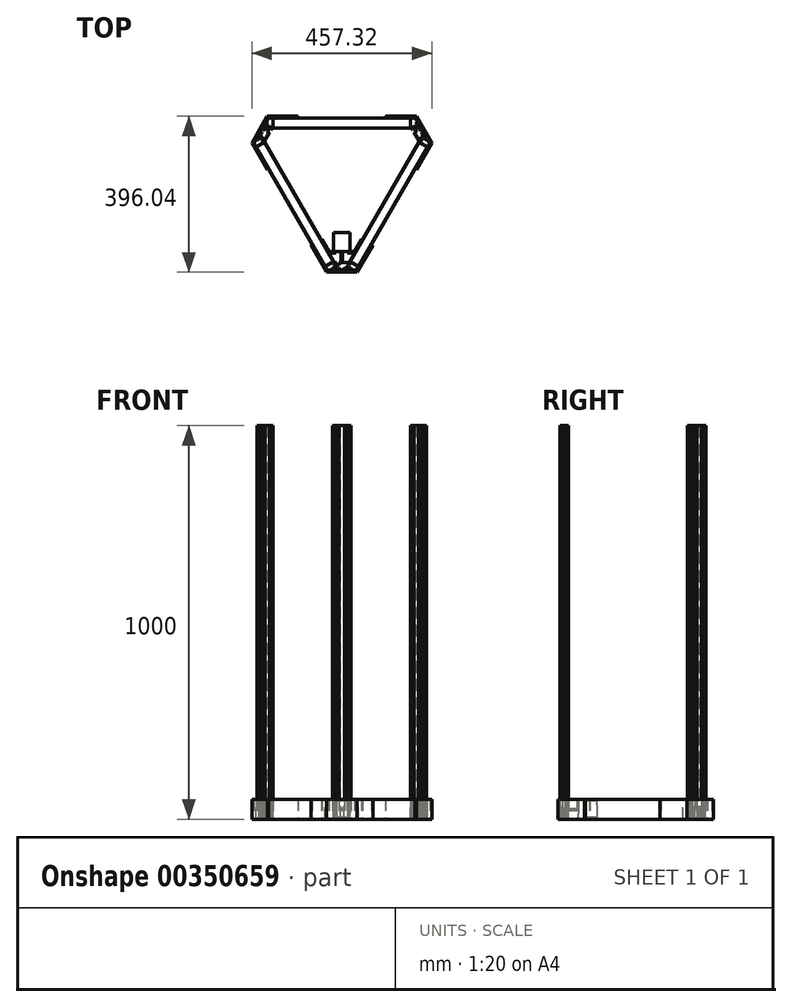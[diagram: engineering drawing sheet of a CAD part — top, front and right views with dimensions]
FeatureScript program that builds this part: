
annotation { "Feature Type Name" : "Feature", "Feature Type Description" : "" }
export const myFeature = defineFeature(function(context is Context, id is Id, definition is map)
    precondition{}
    {
        {
            var Q0;
            Q0=qCreatedBy(makeId("Top.planeOp"),FACE);
            var sketch = newSketch(context, id + "F0", { "sketchPlane" : qUnion([Q0])});
            skLineSegment(sketch, "E0", {"start": v(-75.18, 65.27) * mm, "end": v(-37.5, 0) * mm});
            skLineSegment(sketch, "E1", {"start": v(37.5, 0) * mm, "end": v(75.18, 65.27) * mm});
            skLineSegment(sketch, "E2.0", {"start": v(39.23, -5) * mm, "end": v(78.65, 63.27) * mm});
            skLineSegment(sketch, "E2.2", {"start": v(-78.65, 63.27) * mm, "end": v(-39.23, -5) * mm});
            skLineSegment(sketch, "E3", {"start": v(-78.65, 63.27) * mm, "end": v(-75.18, 65.27) * mm});
            skLineSegment(sketch, "E4", {"start": v(75.18, 65.27) * mm, "end": v(78.65, 63.27) * mm});
            skLineSegment(sketch, "E5", {"start": v(-39.23, -5) * mm, "end": v(39.23, -5) * mm});
            skLineSegment(sketch, "E6", {"start": v(-23.5, 0) * mm, "end": v(-23.5, 7) * mm});
            skLineSegment(sketch, "E7", {"start": v(-23.5, 7) * mm, "end": v(-20, 7) * mm});
            skLineSegment(sketch, "E8", {"start": v(-20, 7) * mm, "end": v(-20, 0) * mm});
            skLineSegment(sketch, "E9", {"start": v(-20, 0) * mm, "end": v(20, 0) * mm});
            skLineSegment(sketch, "E10", {"start": v(20, 0) * mm, "end": v(20, 7) * mm});
            skLineSegment(sketch, "E11", {"start": v(20, 7) * mm, "end": v(23.5, 7) * mm});
            skLineSegment(sketch, "E12", {"start": v(23.5, 7) * mm, "end": v(23.5, 0) * mm});
            skLineSegment(sketch, "E13", {"start": v(-37.5, 0) * mm, "end": v(-23.5, 0) * mm});
            skLineSegment(sketch, "E14", {"start": v(23.5, 0) * mm, "end": v(37.5, 0) * mm});
            skSolve(sketch);
        }
        {
            var Q0;
            Q0 = qSketchRegion(id + "F0", true);
            extrude(context, id + "F1", {"entities" : qUnion([Q0]), "depth" : 50.8 * mm});
        }
        {
            var Q0;
            Q0=qCreatedBy(makeId("Top.planeOp"),FACE);
            var sketch = newSketch(context, id + "F2", { "sketchPlane" : qUnion([Q0])});
            skLineSegment(sketch, "E15", {"start": v(-20, 22.38) * mm, "end": v(-20.8, 22.38) * mm});
            skLineSegment(sketch, "E16", {"start": v(-20.8, 22.38) * mm, "end": v(-23.17, 20) * mm});
            skLineSegment(sketch, "E17", {"start": v(-23.17, 20) * mm, "end": v(-20.8, 17.63) * mm});
            skLineSegment(sketch, "E18", {"start": v(-20.8, 17.63) * mm, "end": v(-20, 17.63) * mm});
            skLineSegment(sketch, "E19", {"start": v(-20, 17.63) * mm, "end": v(-20, 13) * mm});
            skLineSegment(sketch, "E20", {"start": v(-20, 13) * mm, "end": v(-18, 13) * mm});
            skLineSegment(sketch, "E21", {"start": v(-18, 13) * mm, "end": v(-18, 16) * mm});
            skLineSegment(sketch, "E22", {"start": v(-18, 16) * mm, "end": v(-17.06, 16) * mm});
            skLineSegment(sketch, "E23", {"start": v(-17.06, 16) * mm, "end": v(-14, 12.94) * mm});
            skLineSegment(sketch, "E24", {"start": v(-14, 12.94) * mm, "end": v(-14, 7.06) * mm});
            skLineSegment(sketch, "E25", {"start": v(-14, 7.06) * mm, "end": v(-17.06, 4) * mm});
            skLineSegment(sketch, "E26", {"start": v(-17.06, 4) * mm, "end": v(-18, 4) * mm});
            skLineSegment(sketch, "E27", {"start": v(-18, 4) * mm, "end": v(-18, 7) * mm});
            skLineSegment(sketch, "E28", {"start": v(-18, 7) * mm, "end": v(-20, 7) * mm});
            skLineSegment(sketch, "E29", {"start": v(-20, 7) * mm, "end": v(-20, 0) * mm});
            skLineSegment(sketch, "E30", {"start": v(-20, 0) * mm, "end": v(-13, 0) * mm});
            skLineSegment(sketch, "E31", {"start": v(-13, 0) * mm, "end": v(-13, 2) * mm});
            skLineSegment(sketch, "E32", {"start": v(-13, 2) * mm, "end": v(-16, 2) * mm});
            skLineSegment(sketch, "E33", {"start": v(-16, 2) * mm, "end": v(-16, 2.94) * mm});
            skLineSegment(sketch, "E34", {"start": v(-16, 2.94) * mm, "end": v(-12.94, 6) * mm});
            skLineSegment(sketch, "E35", {"start": v(-12.94, 6) * mm, "end": v(-7.06, 6) * mm});
            skLineSegment(sketch, "E36", {"start": v(-7.06, 6) * mm, "end": v(-4, 2.94) * mm});
            skLineSegment(sketch, "E37", {"start": v(-4, 2.94) * mm, "end": v(-4, 2) * mm});
            skLineSegment(sketch, "E38", {"start": v(-4, 2) * mm, "end": v(-7, 2) * mm});
            skLineSegment(sketch, "E39", {"start": v(-7, 2) * mm, "end": v(-7, 0) * mm});
            skLineSegment(sketch, "E40", {"start": v(-7, 0) * mm, "end": v(7, 0) * mm});
            skLineSegment(sketch, "E41", {"start": v(7, 0) * mm, "end": v(7, 2) * mm});
            skLineSegment(sketch, "E42", {"start": v(7, 2) * mm, "end": v(4, 2) * mm});
            skLineSegment(sketch, "E43", {"start": v(4, 2) * mm, "end": v(4, 2.94) * mm});
            skLineSegment(sketch, "E44", {"start": v(4, 2.94) * mm, "end": v(7.06, 6) * mm});
            skLineSegment(sketch, "E45", {"start": v(7.06, 6) * mm, "end": v(12.94, 6) * mm});
            skLineSegment(sketch, "E46", {"start": v(12.94, 6) * mm, "end": v(16, 2.94) * mm});
            skLineSegment(sketch, "E47", {"start": v(16, 2) * mm, "end": v(13, 2) * mm});
            skLineSegment(sketch, "E48", {"start": v(13, 2) * mm, "end": v(13, 0) * mm});
            skLineSegment(sketch, "E49", {"start": v(13, 0) * mm, "end": v(20, 0) * mm});
            skLineSegment(sketch, "E50", {"start": v(20, 0) * mm, "end": v(20, 7) * mm});
            skLineSegment(sketch, "E51", {"start": v(20, 7) * mm, "end": v(18, 7) * mm});
            skLineSegment(sketch, "E52", {"start": v(18, 7) * mm, "end": v(18, 4) * mm});
            skLineSegment(sketch, "E53", {"start": v(18, 4) * mm, "end": v(17.06, 4) * mm});
            skLineSegment(sketch, "E54", {"start": v(17.06, 4) * mm, "end": v(14, 7.06) * mm});
            skLineSegment(sketch, "E55", {"start": v(14, 7.06) * mm, "end": v(14, 12.94) * mm});
            skLineSegment(sketch, "E56", {"start": v(14, 12.94) * mm, "end": v(17.06, 16) * mm});
            skLineSegment(sketch, "E57", {"start": v(17.06, 16) * mm, "end": v(18, 16) * mm});
            skLineSegment(sketch, "E58", {"start": v(18, 16) * mm, "end": v(18, 13) * mm});
            skLineSegment(sketch, "E59", {"start": v(18, 13) * mm, "end": v(20, 13) * mm});
            skLineSegment(sketch, "E60", {"start": v(20, 13) * mm, "end": v(20, 17.63) * mm});
            skLineSegment(sketch, "E61", {"start": v(23.18, 20) * mm, "end": v(20.8, 22.38) * mm});
            skLineSegment(sketch, "E62", {"start": v(20.8, 22.38) * mm, "end": v(20, 22.38) * mm});
            skLineSegment(sketch, "E63", {"start": v(20, 22.38) * mm, "end": v(20, 20) * mm});
            skLineSegment(sketch, "E64", {"start": v(20, 20) * mm, "end": v(-7, 20) * mm});
            skLineSegment(sketch, "E65", {"start": v(-7, 20) * mm, "end": v(-7, 18) * mm});
            skLineSegment(sketch, "E66", {"start": v(-7, 18) * mm, "end": v(-4, 18) * mm});
            skLineSegment(sketch, "E67", {"start": v(-4, 18) * mm, "end": v(-4, 17.06) * mm});
            skLineSegment(sketch, "E68", {"start": v(-4, 17.06) * mm, "end": v(-7.06, 14) * mm});
            skLineSegment(sketch, "E69", {"start": v(-7.06, 14) * mm, "end": v(-12.94, 14) * mm});
            skLineSegment(sketch, "E70", {"start": v(-12.94, 14) * mm, "end": v(-16, 17.06) * mm});
            skLineSegment(sketch, "E71", {"start": v(-16, 17.06) * mm, "end": v(-16, 18) * mm});
            skLineSegment(sketch, "E72", {"start": v(-16, 18) * mm, "end": v(-13, 18) * mm});
            skLineSegment(sketch, "E73", {"start": v(-13, 18) * mm, "end": v(-13, 20) * mm});
            skLineSegment(sketch, "E74", {"start": v(-13, 20) * mm, "end": v(-20, 20) * mm});
            skLineSegment(sketch, "E75", {"start": v(-20, 20) * mm, "end": v(-20, 22.38) * mm});
            skLineSegment(sketch, "E76", {"start": v(23.18, 20) * mm, "end": v(20.8, 17.63) * mm});
            skLineSegment(sketch, "E77", {"start": v(20.8, 17.63) * mm, "end": v(20, 17.63) * mm});
            skLineSegment(sketch, "E78", {"start": v(16, 2.94) * mm, "end": v(16, 2) * mm});
            skSolve(sketch);
        }
        {
            var Q0;
            Q0 = qSketchRegion(id + "F2", true);
            extrude(context, id + "F3", {"entities" : qUnion([Q0]), "depth" : 1000 * mm});
        }
        {
            var Q0;
            Q0=makeQuery(id+"F1.opExtrude","CAP_FACE",FACE,{"disambiguationData":[OSD([sQuery(id+"F0.wireOp",EDGE,"E0"),sQuery(id+"F0.wireOp",EDGE,"E1"),sQuery(id+"F0.wireOp",EDGE,"E2.0"),sQuery(id+"F0.wireOp",EDGE,"E2.2"),sQuery(id+"F0.wireOp",EDGE,"E3"),sQuery(id+"F0.wireOp",EDGE,"E4"),sQuery(id+"F0.wireOp",EDGE,"E5"),sQuery(id+"F0.wireOp",EDGE,"E6"),sQuery(id+"F0.wireOp",EDGE,"E7"),sQuery(id+"F0.wireOp",EDGE,"E8"),sQuery(id+"F0.wireOp",EDGE,"E9"),sQuery(id+"F0.wireOp",EDGE,"E10"),sQuery(id+"F0.wireOp",EDGE,"E11"),sQuery(id+"F0.wireOp",EDGE,"E12")])],"isStart":false});
            var sketch = newSketch(context, id + "F4", { "sketchPlane" : qUnion([Q0])});
            skLineSegment(sketch, "E79", {"start": v(195.98, 325.3) * mm, "end": v(217.98, 312.6) * mm});
            skLineSegment(sketch, "E80", {"start": v(217.98, 312.6) * mm, "end": v(42.98, 9.5) * mm});
            skLineSegment(sketch, "E81", {"start": v(42.98, 9.5) * mm, "end": v(20.98, 22.2) * mm});
            skLineSegment(sketch, "E82", {"start": v(20.98, 22.2) * mm, "end": v(195.98, 325.3) * mm});
            skSolve(sketch);
        }
        {
            var Q0;
            Q0 = qSketchRegion(id + "F4", true);
            var Q1;
            Q1=sQuery(id+"F0.wireOp",VERTEX,"E4.start");
            extrude(context, id + "F5", {"entities" : qUnion([Q0]), "endBound" : BoundingType.UP_TO_VERTEX, "oppositeDirection" : true, "endBoundEntityVertex" : qUnion([Q1]), "depth" : 42.8 * mm});
        }
        {
            var Q0;
            Q0=makeQuery(id+"F5.opExtrude","SWEPT_BODY",BODY,{"disambiguationData":[OSD([sQuery(id+"F4.wireOp",EDGE,"E79"),sQuery(id+"F4.wireOp",EDGE,"E80"),sQuery(id+"F4.wireOp",EDGE,"E81"),sQuery(id+"F4.wireOp",EDGE,"E82")])]});
            var Q1;
            Q1=qCreatedBy(makeId("Right.planeOp"),FACE);
            mirror(context, id + "F6", {"entities" : qUnion([Q0]), "mirrorPlane" : qUnion([Q1])});
        }
        {
            var Q0;
            Q0=makeQuery(id+"F5.opExtrude","SWEPT_FACE",FACE,{"disambiguationData":[OSD([sQuery(id+"F4.wireOp",EDGE,"E79")])]});
            var Q1;
            Q1=makeQuery(id+"F5.opExtrude","SWEPT_FACE",FACE,{"disambiguationData":[OSD([sQuery(id+"F4.wireOp",EDGE,"E81")])]});
            cPlane(context, id + "F7", {"entities" : qUnion([Q0, Q1]), "cplaneType" : CPlaneType.MID_PLANE, "offset" : 25 * mm, "width" : 150 * mm, "height" : 150 * mm});
        }
        {
            var Q0;
            Q0=makeQuery(id+"F6.opPattern","COPY",BODY,{"derivedFrom":makeQuery(id+"F5.opExtrude","SWEPT_BODY",BODY,{"disambiguationData":[OSD([sQuery(id+"F4.wireOp",EDGE,"E79"),sQuery(id+"F4.wireOp",EDGE,"E80"),sQuery(id+"F4.wireOp",EDGE,"E81"),sQuery(id+"F4.wireOp",EDGE,"E82")])]}),"instanceName":"1"});
            var Q1;
            Q1=qCreatedBy(id+"F7.planeOp",FACE);
            mirror(context, id + "F8", {"entities" : qUnion([Q0]), "mirrorPlane" : qUnion([Q1])});
        }
        {
            var Q0;
            Q0=qCreatedBy(makeId("Top.planeOp"),FACE);
            var sketch = newSketch(context, id + "F9", { "sketchPlane" : qUnion([Q0])});
            skLineSegment(sketch, "E83", {"start": v(52.08, 76.06) * mm, "end": v(33.57, 44) * mm});
            skLineSegment(sketch, "E84", {"start": v(-33.57, 44) * mm, "end": v(-52.08, 76.06) * mm});
            skLineSegment(sketch, "E85", {"start": v(-52.08, 76.06) * mm, "end": v(-49.92, 77.31) * mm});
            skLineSegment(sketch, "E86", {"start": v(-49.92, 77.31) * mm, "end": v(-32.42, 47) * mm});
            skLineSegment(sketch, "E87", {"start": v(32.42, 47) * mm, "end": v(49.92, 77.31) * mm});
            skLineSegment(sketch, "E88", {"start": v(49.92, 77.31) * mm, "end": v(52.08, 76.06) * mm});
            skLineSegment(sketch, "E89", {"start": v(33.57, 44) * mm, "end": v(14.42, 44) * mm});
            skLineSegment(sketch, "E90", {"start": v(32.42, 47) * mm, "end": v(14.42, 47) * mm});
            skLineSegment(sketch, "E91", {"start": v(14.42, 47) * mm, "end": v(14.42, 44) * mm});
            skLineSegment(sketch, "E92", {"start": v(-33.57, 44) * mm, "end": v(-14.42, 44) * mm});
            skLineSegment(sketch, "E93", {"start": v(-32.42, 47) * mm, "end": v(-14.42, 47) * mm});
            skLineSegment(sketch, "E94", {"start": v(-14.42, 47) * mm, "end": v(-14.42, 44) * mm});
            skLineSegment(sketch, "E95", {"start": v(-14.42, 44) * mm, "end": v(14.42, 44) * mm, "construction": true});
            skSolve(sketch);
        }
        {
            var Q0;
            Q0 = qSketchRegion(id + "F9", true);
            extrude(context, id + "F10", {"entities" : qUnion([Q0]), "depth" : 50.8 * mm});
        }
        {
            var Q0;
            Q0=makeQuery(id+"F1.opExtrude","SWEPT_BODY",BODY,{"disambiguationData":[OSD([sQuery(id+"F0.wireOp",EDGE,"E0"),sQuery(id+"F0.wireOp",EDGE,"E1"),sQuery(id+"F0.wireOp",EDGE,"E2.0"),sQuery(id+"F0.wireOp",EDGE,"E2.2"),sQuery(id+"F0.wireOp",EDGE,"E3"),sQuery(id+"F0.wireOp",EDGE,"E4"),sQuery(id+"F0.wireOp",EDGE,"E5"),sQuery(id+"F0.wireOp",EDGE,"E6"),sQuery(id+"F0.wireOp",EDGE,"E7"),sQuery(id+"F0.wireOp",EDGE,"E8"),sQuery(id+"F0.wireOp",EDGE,"E9"),sQuery(id+"F0.wireOp",EDGE,"E10"),sQuery(id+"F0.wireOp",EDGE,"E11"),sQuery(id+"F0.wireOp",EDGE,"E12")])]});
            var Q1;
            Q1=qCreatedBy(id+"F7.planeOp",FACE);
            mirror(context, id + "F11", {"entities" : qUnion([Q0]), "mirrorPlane" : qUnion([Q1])});
        }
        {
            var Q0;
            Q0=makeQuery(id+"F11.opPattern","COPY",BODY,{"derivedFrom":makeQuery(id+"F1.opExtrude","SWEPT_BODY",BODY,{"disambiguationData":[OSD([sQuery(id+"F0.wireOp",EDGE,"E0"),sQuery(id+"F0.wireOp",EDGE,"E1"),sQuery(id+"F0.wireOp",EDGE,"E2.0"),sQuery(id+"F0.wireOp",EDGE,"E2.2"),sQuery(id+"F0.wireOp",EDGE,"E3"),sQuery(id+"F0.wireOp",EDGE,"E4"),sQuery(id+"F0.wireOp",EDGE,"E5"),sQuery(id+"F0.wireOp",EDGE,"E6"),sQuery(id+"F0.wireOp",EDGE,"E7"),sQuery(id+"F0.wireOp",EDGE,"E8"),sQuery(id+"F0.wireOp",EDGE,"E9"),sQuery(id+"F0.wireOp",EDGE,"E10"),sQuery(id+"F0.wireOp",EDGE,"E11"),sQuery(id+"F0.wireOp",EDGE,"E12")])]}),"instanceName":"1"});
            var Q1;
            Q1=qCreatedBy(makeId("Right.planeOp"),FACE);
            mirror(context, id + "F12", {"entities" : qUnion([Q0]), "mirrorPlane" : qUnion([Q1])});
        }
        {
            var Q0;
            Q0=makeQuery(id+"F3.opExtrude","SWEPT_BODY",BODY,{"disambiguationData":[OSD([sQuery(id+"F2.wireOp",EDGE,"E15"),sQuery(id+"F2.wireOp",EDGE,"E16"),sQuery(id+"F2.wireOp",EDGE,"E17"),sQuery(id+"F2.wireOp",EDGE,"E18"),sQuery(id+"F2.wireOp",EDGE,"E19"),sQuery(id+"F2.wireOp",EDGE,"E20"),sQuery(id+"F2.wireOp",EDGE,"E21"),sQuery(id+"F2.wireOp",EDGE,"E22"),sQuery(id+"F2.wireOp",EDGE,"E23"),sQuery(id+"F2.wireOp",EDGE,"E24"),sQuery(id+"F2.wireOp",EDGE,"E25"),sQuery(id+"F2.wireOp",EDGE,"E26"),sQuery(id+"F2.wireOp",EDGE,"E27"),sQuery(id+"F2.wireOp",EDGE,"E28"),sQuery(id+"F2.wireOp",EDGE,"E29"),sQuery(id+"F2.wireOp",EDGE,"E30"),sQuery(id+"F2.wireOp",EDGE,"E31"),sQuery(id+"F2.wireOp",EDGE,"E32"),sQuery(id+"F2.wireOp",EDGE,"E33"),sQuery(id+"F2.wireOp",EDGE,"E34"),sQuery(id+"F2.wireOp",EDGE,"E35"),sQuery(id+"F2.wireOp",EDGE,"E36"),sQuery(id+"F2.wireOp",EDGE,"E37"),sQuery(id+"F2.wireOp",EDGE,"E38"),sQuery(id+"F2.wireOp",EDGE,"E39"),sQuery(id+"F2.wireOp",EDGE,"E40"),sQuery(id+"F2.wireOp",EDGE,"E41"),sQuery(id+"F2.wireOp",EDGE,"E42"),sQuery(id+"F2.wireOp",EDGE,"E43"),sQuery(id+"F2.wireOp",EDGE,"E44"),sQuery(id+"F2.wireOp",EDGE,"E45"),sQuery(id+"F2.wireOp",EDGE,"E46"),sQuery(id+"F2.wireOp",EDGE,"E47"),sQuery(id+"F2.wireOp",EDGE,"E48"),sQuery(id+"F2.wireOp",EDGE,"E49"),sQuery(id+"F2.wireOp",EDGE,"E50"),sQuery(id+"F2.wireOp",EDGE,"E51"),sQuery(id+"F2.wireOp",EDGE,"E52"),sQuery(id+"F2.wireOp",EDGE,"E53"),sQuery(id+"F2.wireOp",EDGE,"E54"),sQuery(id+"F2.wireOp",EDGE,"E55"),sQuery(id+"F2.wireOp",EDGE,"E56"),sQuery(id+"F2.wireOp",EDGE,"E57"),sQuery(id+"F2.wireOp",EDGE,"E58"),sQuery(id+"F2.wireOp",EDGE,"E59"),sQuery(id+"F2.wireOp",EDGE,"E60"),sQuery(id+"F2.wireOp",EDGE,"E61"),sQuery(id+"F2.wireOp",EDGE,"E62"),sQuery(id+"F2.wireOp",EDGE,"E63"),sQuery(id+"F2.wireOp",EDGE,"E64"),sQuery(id+"F2.wireOp",EDGE,"E65"),sQuery(id+"F2.wireOp",EDGE,"E66"),sQuery(id+"F2.wireOp",EDGE,"E67"),sQuery(id+"F2.wireOp",EDGE,"E68"),sQuery(id+"F2.wireOp",EDGE,"E69"),sQuery(id+"F2.wireOp",EDGE,"E70"),sQuery(id+"F2.wireOp",EDGE,"E71"),sQuery(id+"F2.wireOp",EDGE,"E72"),sQuery(id+"F2.wireOp",EDGE,"E73"),sQuery(id+"F2.wireOp",EDGE,"E74"),sQuery(id+"F2.wireOp",EDGE,"E75"),sQuery(id+"F2.wireOp",EDGE,"E76"),sQuery(id+"F2.wireOp",EDGE,"E77"),sQuery(id+"F2.wireOp",EDGE,"E78")])]});
            var Q1;
            Q1=qCreatedBy(id+"F7.planeOp",FACE);
            mirror(context, id + "F13", {"entities" : qUnion([Q0]), "mirrorPlane" : qUnion([Q1])});
        }
        {
            var Q0;
            Q0=makeQuery(id+"F13.opPattern","COPY",BODY,{"derivedFrom":makeQuery(id+"F3.opExtrude","SWEPT_BODY",BODY,{"disambiguationData":[OSD([sQuery(id+"F2.wireOp",EDGE,"E15"),sQuery(id+"F2.wireOp",EDGE,"E16"),sQuery(id+"F2.wireOp",EDGE,"E17"),sQuery(id+"F2.wireOp",EDGE,"E18"),sQuery(id+"F2.wireOp",EDGE,"E19"),sQuery(id+"F2.wireOp",EDGE,"E20"),sQuery(id+"F2.wireOp",EDGE,"E21"),sQuery(id+"F2.wireOp",EDGE,"E22"),sQuery(id+"F2.wireOp",EDGE,"E23"),sQuery(id+"F2.wireOp",EDGE,"E24"),sQuery(id+"F2.wireOp",EDGE,"E25"),sQuery(id+"F2.wireOp",EDGE,"E26"),sQuery(id+"F2.wireOp",EDGE,"E27"),sQuery(id+"F2.wireOp",EDGE,"E28"),sQuery(id+"F2.wireOp",EDGE,"E29"),sQuery(id+"F2.wireOp",EDGE,"E30"),sQuery(id+"F2.wireOp",EDGE,"E31"),sQuery(id+"F2.wireOp",EDGE,"E32"),sQuery(id+"F2.wireOp",EDGE,"E33"),sQuery(id+"F2.wireOp",EDGE,"E34"),sQuery(id+"F2.wireOp",EDGE,"E35"),sQuery(id+"F2.wireOp",EDGE,"E36"),sQuery(id+"F2.wireOp",EDGE,"E37"),sQuery(id+"F2.wireOp",EDGE,"E38"),sQuery(id+"F2.wireOp",EDGE,"E39"),sQuery(id+"F2.wireOp",EDGE,"E40"),sQuery(id+"F2.wireOp",EDGE,"E41"),sQuery(id+"F2.wireOp",EDGE,"E42"),sQuery(id+"F2.wireOp",EDGE,"E43"),sQuery(id+"F2.wireOp",EDGE,"E44"),sQuery(id+"F2.wireOp",EDGE,"E45"),sQuery(id+"F2.wireOp",EDGE,"E46"),sQuery(id+"F2.wireOp",EDGE,"E47"),sQuery(id+"F2.wireOp",EDGE,"E48"),sQuery(id+"F2.wireOp",EDGE,"E49"),sQuery(id+"F2.wireOp",EDGE,"E50"),sQuery(id+"F2.wireOp",EDGE,"E51"),sQuery(id+"F2.wireOp",EDGE,"E52"),sQuery(id+"F2.wireOp",EDGE,"E53"),sQuery(id+"F2.wireOp",EDGE,"E54"),sQuery(id+"F2.wireOp",EDGE,"E55"),sQuery(id+"F2.wireOp",EDGE,"E56"),sQuery(id+"F2.wireOp",EDGE,"E57"),sQuery(id+"F2.wireOp",EDGE,"E58"),sQuery(id+"F2.wireOp",EDGE,"E59"),sQuery(id+"F2.wireOp",EDGE,"E60"),sQuery(id+"F2.wireOp",EDGE,"E61"),sQuery(id+"F2.wireOp",EDGE,"E62"),sQuery(id+"F2.wireOp",EDGE,"E63"),sQuery(id+"F2.wireOp",EDGE,"E64"),sQuery(id+"F2.wireOp",EDGE,"E65"),sQuery(id+"F2.wireOp",EDGE,"E66"),sQuery(id+"F2.wireOp",EDGE,"E67"),sQuery(id+"F2.wireOp",EDGE,"E68"),sQuery(id+"F2.wireOp",EDGE,"E69"),sQuery(id+"F2.wireOp",EDGE,"E70"),sQuery(id+"F2.wireOp",EDGE,"E71"),sQuery(id+"F2.wireOp",EDGE,"E72"),sQuery(id+"F2.wireOp",EDGE,"E73"),sQuery(id+"F2.wireOp",EDGE,"E74"),sQuery(id+"F2.wireOp",EDGE,"E75"),sQuery(id+"F2.wireOp",EDGE,"E76"),sQuery(id+"F2.wireOp",EDGE,"E77"),sQuery(id+"F2.wireOp",EDGE,"E78")])]}),"instanceName":"1"});
            var Q1;
            Q1=qCreatedBy(makeId("Right.planeOp"),FACE);
            mirror(context, id + "F14", {"entities" : qUnion([Q0]), "mirrorPlane" : qUnion([Q1])});
        }
        {
            var Q0;
            Q0=makeQuery(id+"F10.opExtrude","SWEPT_FACE",FACE,{"disambiguationData":[OSD([sQuery(id+"F9.wireOp",EDGE,"E90")])]});
            var sketch = newSketch(context, id + "F15", { "sketchPlane" : qUnion([Q0])});
            skLineSegment(sketch, "E96.bottom", {"start": v(-21.15, 46.55) * mm, "end": v(21.15, 46.55) * mm});
            skLineSegment(sketch, "E96.top", {"start": v(-21.15, 4.25) * mm, "end": v(21.15, 4.25) * mm});
            skLineSegment(sketch, "E96.left", {"start": v(-21.15, 46.55) * mm, "end": v(-21.15, 4.25) * mm});
            skLineSegment(sketch, "E96.right", {"start": v(21.15, 46.55) * mm, "end": v(21.15, 4.25) * mm});
            skSolve(sketch);
        }
        {
            var Q0;
            Q0 = qSketchRegion(id + "F15", true);
            extrude(context, id + "F16", {"entities" : qUnion([Q0]), "depth" : 48 * mm});
        }
        {
            var Q0;
            Q0=makeQuery(id+"F16.opExtrude","CAP_FACE",FACE,{"disambiguationData":[OSD([sQuery(id+"F15.wireOp",EDGE,"E96.bottom"),sQuery(id+"F15.wireOp",EDGE,"E96.top"),sQuery(id+"F15.wireOp",EDGE,"E96.left"),sQuery(id+"F15.wireOp",EDGE,"E96.right")])],"isStart":true});
            var sketch = newSketch(context, id + "F17", { "sketchPlane" : qUnion([Q0])});
            skCircle(sketch, "E97", {"center": v(0, 25.4) * mm, "radius": 2.44 * mm});
            skLineSegment(sketch, "E98", {"start": v(21.15, 25.4) * mm, "end": v(-21.15, 25.4) * mm, "construction": true});
            skSolve(sketch);
        }
        {
            var Q0;
            Q0 = qSketchRegion(id + "F17", true);
            extrude(context, id + "F18", {"entities" : qUnion([Q0]), "operationType" : NewBodyOperationType.ADD, "depth" : 24 * mm});
        }
        {
            var Q0;
            Q0=makeQuery(id+"F16.opExtrude","SWEPT_EDGE",EDGE,{"disambiguationData":[OSD([sQuery(id+"F15.wireOp",EDGE,"E96.bottom"),sQuery(id+"F15.wireOp",EDGE,"E96.left")])]});
            var Q1;
            Q1=makeQuery(id+"F16.opExtrude","SWEPT_EDGE",EDGE,{"disambiguationData":[OSD([sQuery(id+"F15.wireOp",EDGE,"E96.top"),sQuery(id+"F15.wireOp",EDGE,"E96.left")])]});
            var Q2;
            Q2=makeQuery(id+"F16.opExtrude","SWEPT_EDGE",EDGE,{"disambiguationData":[OSD([sQuery(id+"F15.wireOp",EDGE,"E96.top"),sQuery(id+"F15.wireOp",EDGE,"E96.right")])]});
            var Q3;
            Q3=makeQuery(id+"F16.opExtrude","SWEPT_EDGE",EDGE,{"disambiguationData":[OSD([sQuery(id+"F15.wireOp",EDGE,"E96.bottom"),sQuery(id+"F15.wireOp",EDGE,"E96.right")])]});
            fillet(context, id + "F19", {"entities" : qUnion([Q0, Q1, Q2, Q3]), "radius" : 10 * mm, "tangentPropagation" : true, "allowEdgeOverflow" : false});
        }
    });
